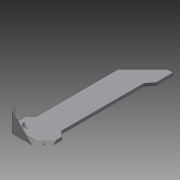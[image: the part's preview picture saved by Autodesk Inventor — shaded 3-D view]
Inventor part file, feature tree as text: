
AUTODESK INVENTOR PART (.ipt)
format: ipt  version: 2014 SP1 (Build 180222100, 222)  size: 158,208 bytes
history: native  units: in
note: dims shown in document units (in); Inventor stores cm internally (conversion verified against a paired STEP export)
features: extrude x4, sketch x4, plane x1, reference x1, projected_geometry x1
ambient origin geometry x8: Origin, YZ Plane, XZ Plane, XY Plane, X Axis, Y Axis, Z Axis, Center Point
bodies: Solid1 (feature_tree)
feature tree (11):
  plane  "Work Plane1"
  extrude  "Extrusion1"  Depth=0.4134in
  extrude  "Extrusion2"  Depth=0.374in
  extrude  "Extrusion3"  Depth=0.0453in
  extrude  "Extrusion4"  Depth=2.1457in
  sketch  "Sketch1"  dims[d2=0.4134in d4=0.1673in]
  reference  "Reference1"
  sketch  "Sketch2"  dims[d6=0.2067in d7=0.374in]
  sketch  "Sketch3"  dims[d8=0.0453in d9=0.0in d10=0.0453in]
  sketch  "Sketch4"  dims[d11=0.0591in d12=0.0in d13=2.1457in d15=0.2953in d16=0.2756in d17=0.3937in d18=1.3583in d19=0.2067in d20=0.315in d21=0.2953in d22=0.0453in d23=0.0in d24=0.0886in d25=0.2264in d26=0.0886in d27=0.1772in d28=0.0886in d29=0.1772in d30=0.187in d32=0.2264in d33=0.1772in d34=0.0886in d35=0.0886in d36=0.0886in d37=0.5906in d38=0.0453in d39=0.0in]
  projected_geometry  "Projected Loop1"
